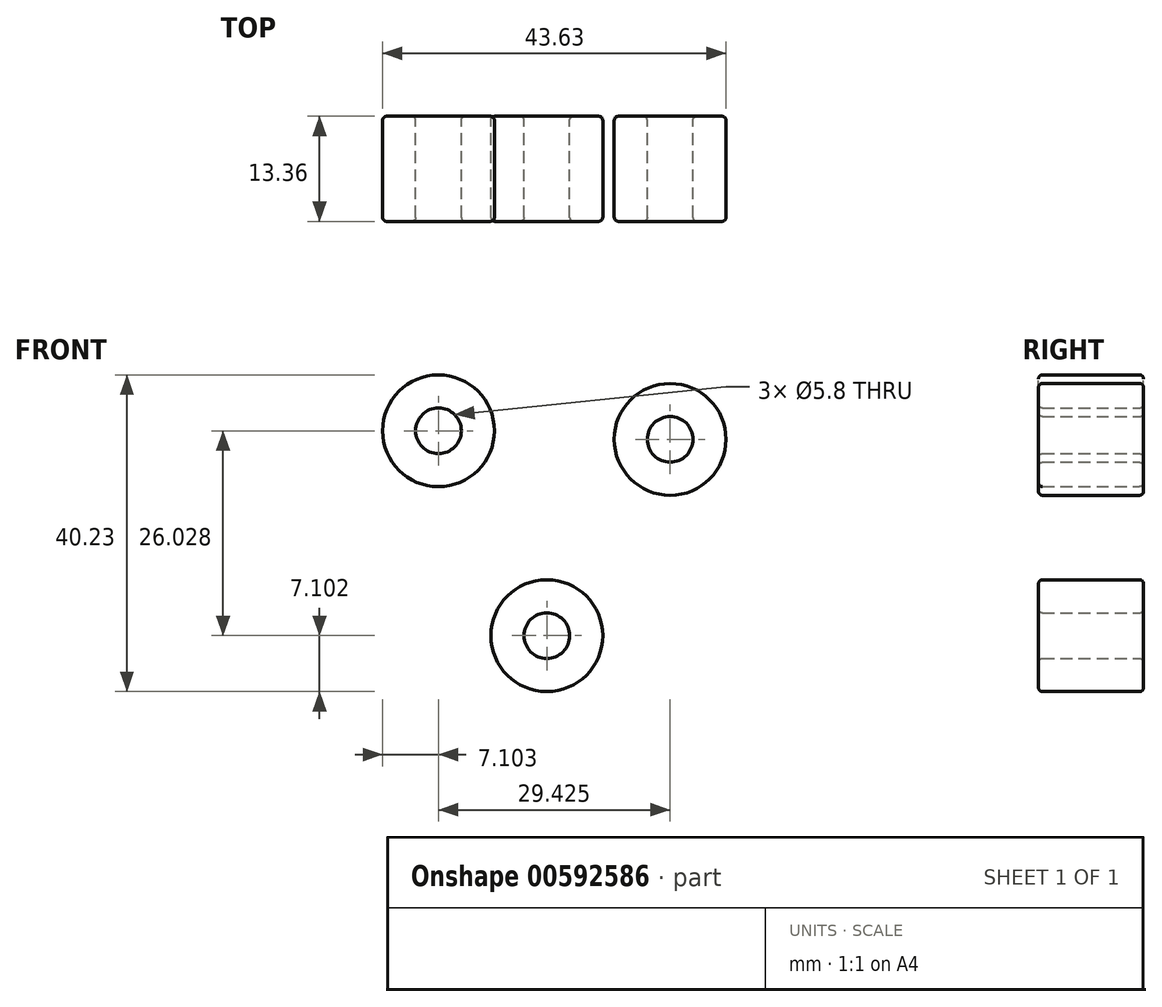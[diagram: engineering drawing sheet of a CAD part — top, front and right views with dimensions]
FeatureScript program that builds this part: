
annotation { "Feature Type Name" : "Feature", "Feature Type Description" : "" }
export const myFeature = defineFeature(function(context is Context, id is Id, definition is map)
    precondition{}
    {
        {
            assignVariable(context, id + "F0", {"name" : "Wheel_len", "anyValue" : 13.35 * mm});
        }
        {
            var Q0;
            Q0=qCreatedBy(makeId("Front.planeOp"),FACE);
            var sketch = newSketch(context, id + "F1", { "sketchPlane" : qUnion([Q0])});
            skCircle(sketch, "E0", {"center": v(0, 0) * mm, "radius": 22.15 * mm, "construction": true});
            skCircle(sketch, "E1", {"center": v(0, 0) * mm, "radius": 6.8 * mm});
            skCircle(sketch, "E2", {"center": v(0, 0) * mm, "radius": 8.9 * mm, "construction": true});
            skLineSegment(sketch, "E3.bottom", {"start": v(1.35, 4) * mm, "end": v(-1.35, 4) * mm});
            skLineSegment(sketch, "E3.top", {"start": v(1.35, -4) * mm, "end": v(-1.35, -4) * mm});
            skLineSegment(sketch, "E3.left", {"start": v(1.35, 4) * mm, "end": v(1.35, -4) * mm, "construction": true});
            skLineSegment(sketch, "E3.right", {"start": v(-1.35, 4) * mm, "end": v(-1.35, -4) * mm, "construction": true});
            skLineSegment(sketch, "E4.bottom", {"start": v(4, 1.35) * mm, "end": v(-4, 1.35) * mm, "construction": true});
            skLineSegment(sketch, "E4.top", {"start": v(4, -1.35) * mm, "end": v(-4, -1.35) * mm, "construction": true});
            skLineSegment(sketch, "E4.left", {"start": v(4, 1.35) * mm, "end": v(4, -1.35) * mm});
            skLineSegment(sketch, "E4.right", {"start": v(-4, 1.35) * mm, "end": v(-4, -1.35) * mm});
            skLineSegment(sketch, "E5", {"start": v(-1.35, 4) * mm, "end": v(-1.35, 1.35) * mm});
            skLineSegment(sketch, "E6", {"start": v(-1.35, 1.35) * mm, "end": v(-4, 1.35) * mm});
            skLineSegment(sketch, "E7", {"start": v(-4, -1.35) * mm, "end": v(-1.35, -1.35) * mm});
            skLineSegment(sketch, "E8", {"start": v(-1.35, -1.35) * mm, "end": v(-1.35, -4) * mm});
            skLineSegment(sketch, "E9", {"start": v(1.35, -4) * mm, "end": v(1.35, -1.35) * mm});
            skLineSegment(sketch, "E10", {"start": v(1.35, -1.35) * mm, "end": v(4, -1.35) * mm});
            skLineSegment(sketch, "E11", {"start": v(4, 1.35) * mm, "end": v(1.35, 1.35) * mm});
            skLineSegment(sketch, "E12", {"start": v(1.35, 1.35) * mm, "end": v(1.35, 4) * mm});
            skCircle(sketch, "E13", {"center": v(0, 0) * mm, "radius": 3 * mm, "construction": true});
            skCircle(sketch, "E14", {"center": v(-14.4, 9.04) * mm, "radius": 7.1 * mm});
            skLineSegment(sketch, "E15", {"start": v(0, 0) * mm, "end": v(-14.4, 9.04) * mm, "construction": true});
            skCircle(sketch, "E16", {"center": v(0, 0) * mm, "radius": 7.1 * mm, "construction": true});
            skCircle(sketch, "E17", {"center": v(-14.4, 9.04) * mm, "radius": 2.8 * mm});
            skCircle(sketch, "E18.0", {"center": v(-14.4, 9.04) * mm, "radius": 2.9 * mm});
            skCircle(sketch, "E19.1.0", {"center": v(-0.63, -16.99) * mm, "radius": 7.1 * mm});
            skCircle(sketch, "E19.1.1", {"center": v(-0.63, -16.99) * mm, "radius": 2.9 * mm});
            skCircle(sketch, "E19.1.2", {"center": v(-0.63, -16.99) * mm, "radius": 2.8 * mm});
            skLineSegment(sketch, "E19.1.3", {"start": v(0, 0) * mm, "end": v(-0.63, -16.99) * mm, "construction": true});
            skCircle(sketch, "E19.2.0", {"center": v(15.03, 7.95) * mm, "radius": 7.1 * mm});
            skCircle(sketch, "E19.2.1", {"center": v(15.03, 7.95) * mm, "radius": 2.9 * mm});
            skCircle(sketch, "E19.2.2", {"center": v(15.03, 7.95) * mm, "radius": 2.8 * mm});
            skLineSegment(sketch, "E19.2.3", {"start": v(0, 0) * mm, "end": v(15.03, 7.95) * mm, "construction": true});
            skCircle(sketch, "E20", {"center": v(0, 17) * mm, "radius": 3 * mm});
            skCircle(sketch, "E21", {"center": v(0, 0) * mm, "radius": 17 * mm, "construction": true});
            skCircle(sketch, "E22.1.0", {"center": v(-14.72, -8.5) * mm, "radius": 3 * mm});
            skCircle(sketch, "E22.2.0", {"center": v(14.72, -8.5) * mm, "radius": 3 * mm});
            skSolve(sketch);
        }
        {
            var Q0;
            Q0=makeQuery(id+"F1.imprint","IMPRINT",FACE,{"disambiguationData":[TD([[makeQuery(id+"F1.imprint","IMPRINT",EDGE,{"derivedFrom":sQuery(id+"F1.wireOp",EDGE,"E19.2.0")}),1.0]])]});
            var Q1;
            Q1=makeQuery(id+"F1.imprint","IMPRINT",FACE,{"disambiguationData":[TD([[makeQuery(id+"F1.imprint","IMPRINT",EDGE,{"derivedFrom":sQuery(id+"F1.wireOp",EDGE,"E14")}),1.0]])]});
            var Q2;
            Q2=makeQuery(id+"F1.imprint","IMPRINT",FACE,{"disambiguationData":[TD([[makeQuery(id+"F1.imprint","IMPRINT",EDGE,{"derivedFrom":sQuery(id+"F1.wireOp",EDGE,"E19.1.0")}),1.0]])]});
            extrude(context, id + "F2", {"entities" : qUnion([Q0, Q1, Q2]), "endBound" : BoundingType.SYMMETRIC, "depth" : getVariable(context, 'Wheel_len'), "offsetDistance" : 25.4 * mm});
        }
        {
            var Q0;
            Q0=makeQuery(id+"F2.opExtrude","CAP_EDGE",EDGE,{"disambiguationData":[OSD([sQuery(id+"F1.wireOp",EDGE,"E14")])],"isStart":true});
            var Q1;
            Q1=makeQuery(id+"F2.opExtrude","CAP_EDGE",EDGE,{"disambiguationData":[OSD([sQuery(id+"F1.wireOp",EDGE,"E19.2.0")])],"isStart":true});
            var Q2;
            Q2=makeQuery(id+"F2.opExtrude","CAP_EDGE",EDGE,{"disambiguationData":[OSD([sQuery(id+"F1.wireOp",EDGE,"E19.1.0")])],"isStart":true});
            var Q3;
            Q3=makeQuery(id+"F2.opExtrude","CAP_EDGE",EDGE,{"disambiguationData":[OSD([sQuery(id+"F1.wireOp",EDGE,"E19.1.0")])],"isStart":false});
            var Q4;
            Q4=makeQuery(id+"F2.opExtrude","CAP_EDGE",EDGE,{"disambiguationData":[OSD([sQuery(id+"F1.wireOp",EDGE,"E14")])],"isStart":false});
            var Q5;
            Q5=makeQuery(id+"F2.opExtrude","CAP_EDGE",EDGE,{"disambiguationData":[OSD([sQuery(id+"F1.wireOp",EDGE,"E19.2.0")])],"isStart":false});
            fillet(context, id + "F3", {"entities" : qUnion([Q0, Q1, Q2, Q3, Q4, Q5]), "radius" : 0.5 * mm, "tangentPropagation" : true, "allowEdgeOverflow" : false});
        }
        {
            var Q0;
            Q0=makeQuery(id+"F2.opExtrude","CAP_EDGE",EDGE,{"disambiguationData":[OSD([sQuery(id+"F1.wireOp",EDGE,"E19.2.1")])],"isStart":false});
            var Q1;
            Q1=makeQuery(id+"F2.opExtrude","CAP_EDGE",EDGE,{"disambiguationData":[OSD([sQuery(id+"F1.wireOp",EDGE,"E19.1.1")])],"isStart":false});
            var Q2;
            Q2=makeQuery(id+"F2.opExtrude","CAP_EDGE",EDGE,{"disambiguationData":[OSD([sQuery(id+"F1.wireOp",EDGE,"E18.0")])],"isStart":false});
            var Q3;
            Q3=makeQuery(id+"F2.opExtrude","CAP_EDGE",EDGE,{"disambiguationData":[OSD([sQuery(id+"F1.wireOp",EDGE,"E18.0")])],"isStart":true});
            var Q4;
            Q4=makeQuery(id+"F2.opExtrude","CAP_EDGE",EDGE,{"disambiguationData":[OSD([sQuery(id+"F1.wireOp",EDGE,"E19.2.1")])],"isStart":true});
            var Q5;
            Q5=makeQuery(id+"F2.opExtrude","CAP_EDGE",EDGE,{"disambiguationData":[OSD([sQuery(id+"F1.wireOp",EDGE,"E19.1.1")])],"isStart":true});
            fillet(context, id + "F4", {"entities" : qUnion([Q0, Q1, Q2, Q3, Q4, Q5]), "radius" : 0.5 * mm, "tangentPropagation" : true, "allowEdgeOverflow" : false});
        }
    });
